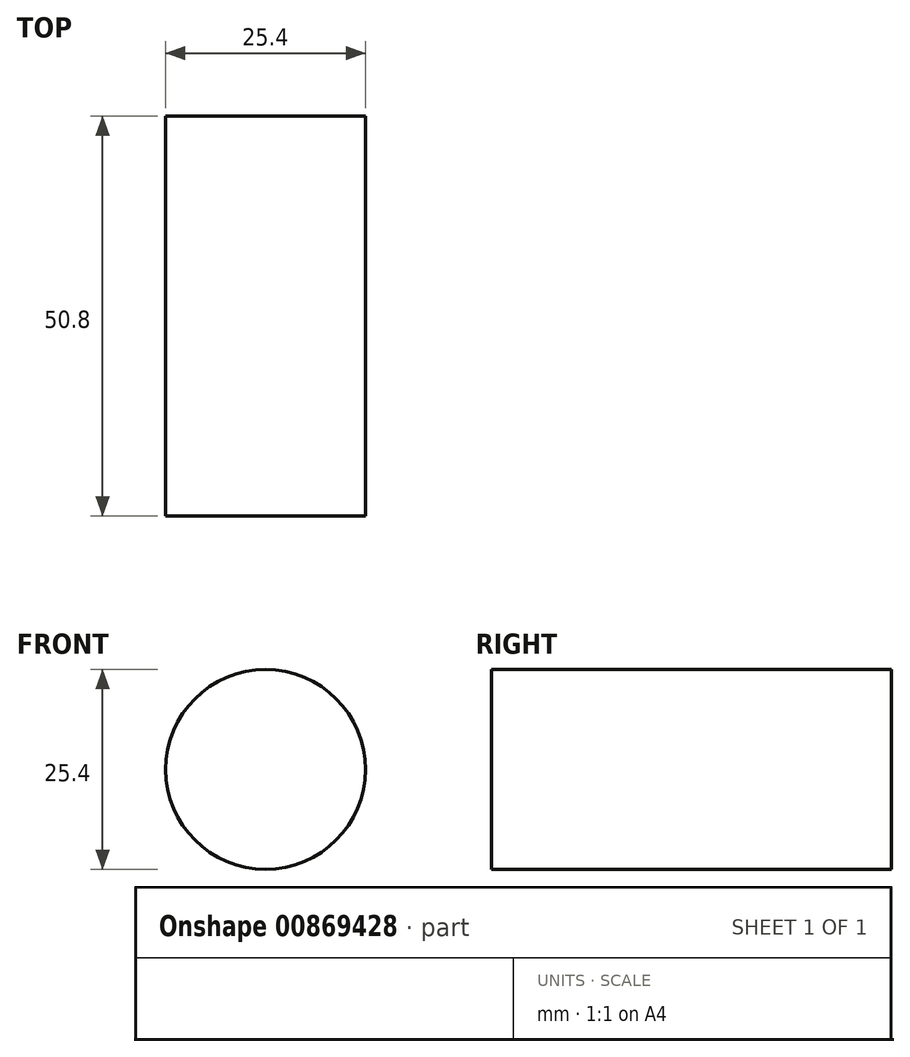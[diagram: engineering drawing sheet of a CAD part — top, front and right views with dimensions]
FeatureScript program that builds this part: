
annotation { "Feature Type Name" : "Feature", "Feature Type Description" : "" }
export const myFeature = defineFeature(function(context is Context, id is Id, definition is map)
    precondition{}
    {
        {
            var Q0;
            Q0=qCreatedBy(makeId("Front.planeOp"),FACE);
            var sketch = newSketch(context, id + "F0", { "sketchPlane" : qUnion([Q0])});
            skCircle(sketch, "E0", {"center": v(0, 0) * mm, "radius": 12.7 * mm});
            skSolve(sketch);
        }
        {
            var Q0;
            Q0 = qSketchRegion(id + "F0", true);
            extrude(context, id + "F1", {"entities" : qUnion([Q0]), "depth" : 50.8 * mm, "offsetDistance" : 25.4 * mm});
        }
    });
